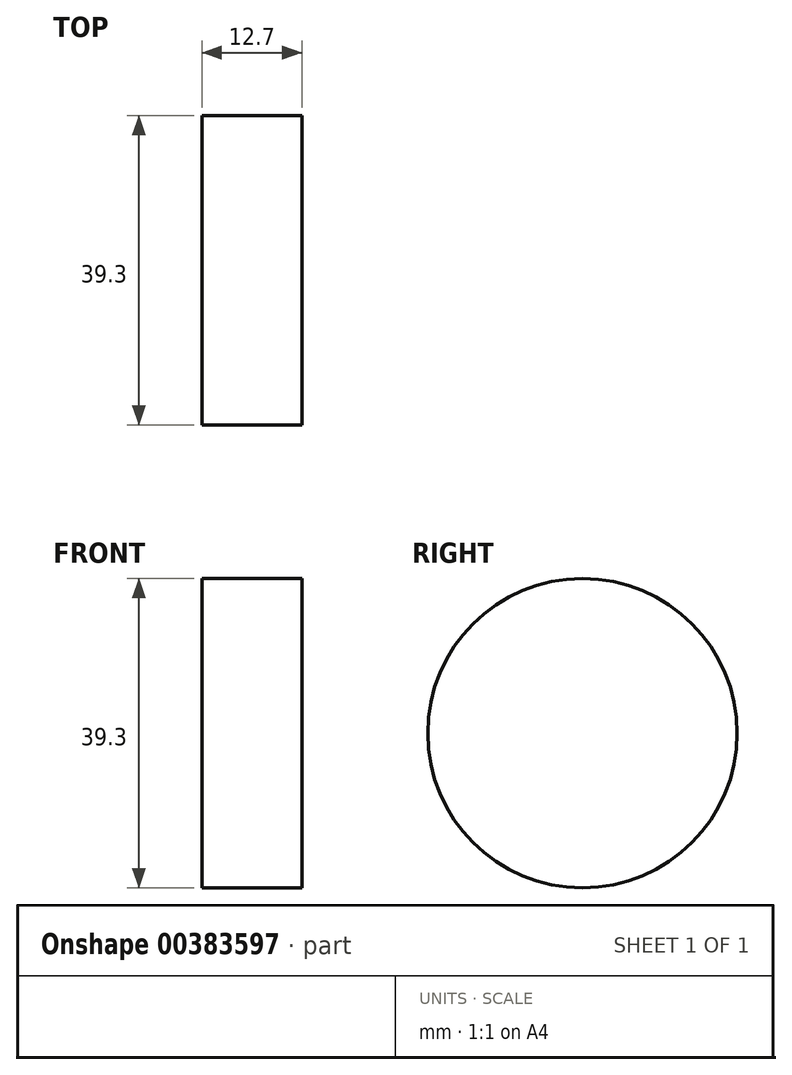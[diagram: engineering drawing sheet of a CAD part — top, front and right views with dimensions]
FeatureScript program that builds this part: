
annotation { "Feature Type Name" : "Feature", "Feature Type Description" : "" }
export const myFeature = defineFeature(function(context is Context, id is Id, definition is map)
    precondition{}
    {
        {
            var Q0;
            Q0=qCreatedBy(makeId("Right.planeOp"),FACE);
            var sketch = newSketch(context, id + "F0", { "sketchPlane" : qUnion([Q0])});
            skCircle(sketch, "E0", {"center": v(-43.92, 0) * mm, "radius": 19.65 * mm});
            skSolve(sketch);
        }
        {
            var Q0;
            Q0=makeQuery(id+"F0.imprint","IMPRINT",FACE,{"disambiguationData":[TD([[makeQuery(id+"F0.imprint","IMPRINT",EDGE,{"derivedFrom":sQuery(id+"F0.wireOp",EDGE,"E0")}),1.0]])]});
            extrude(context, id + "F1", {"entities" : qUnion([Q0]), "oppositeDirection" : true, "depth" : 12.7 * mm});
        }
    });
